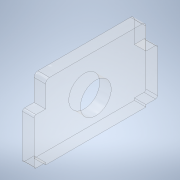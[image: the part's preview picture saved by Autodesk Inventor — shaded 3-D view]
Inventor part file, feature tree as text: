
AUTODESK INVENTOR PART (.ipt)
format: ipt  version: 2021 (Build 250183000, 183)  size: 184,320 bytes
history: native  units: mm
features: extrude x1, fillet x1, sketch x1
ambient origin geometry x8: Origin, YZ Plane, XZ Plane, XY Plane, X Axis, Y Axis, Z Axis, Center Point
bodies: Solid1 (feature_tree)
feature tree (3):
  extrude  "Extrusion1"  Depth=3.0mm TaperAngle=0.0deg
  fillet  "Fillet1"  Radius=1.45mm
  sketch  "Sketch1"  dims[d2=8.1mm d9=3.0mm d10=0.0mm d22=1.45mm d29=6.5mm d30=6.5mm d31=2.8mm d33=7.45mm d36=0.5mm d39=2.0mm d40=2.0mm d42=12.0mm d43=12.0mm d45=12.0mm d46=1.75mm d47=1.75mm d51=25.2mm d54=32.0mm d55=19.0mm d56=3.0mm d57=3.0mm d58=6.6mm d59=8.0mm d60=2.0mm d61=0.5mm d64=0.55mm d65=8.0mm d66=1.0mm d67=0.5mm]
